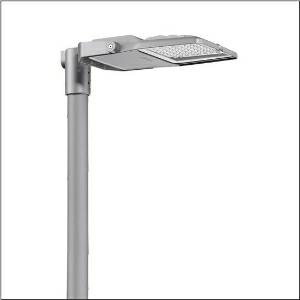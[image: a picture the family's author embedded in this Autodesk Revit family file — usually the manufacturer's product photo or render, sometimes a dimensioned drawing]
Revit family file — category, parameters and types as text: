
# Revit family: floodlight_fl_21_mini___pl52_5xa7776d2d3a_85e1
name_source: partatom
category: Lighting Fixtures
units: mm (PartAtom-declared; Revit-internal decimal feet)

## family parameters
Cut with Voids When Loaded = No
Host = Face
Light Source = No
Part Type = Normal
Room Calculation Point = No
Round Connector Dimension = Use Diameter
Shared = No

## types (1)
- --- (1 x LED, 17840 lm, 142.9 W, 3000K)
    Apparent Load = 143 VA
    CIE Flux Codes = 26 60 98 100 100
    Color Rendering = 70
    Color Temperature = 3000K
    Default Elevation = 1800 mm
    Description = Floodlight FL 21 mini, floodlight, primary light control with lens, of PMMA, primary optical cover: protective disc, of toughened safety glass, transparent, light distribution: PL52, light emission: direct distribution, installation type: surface-mounted, LED, High Power LED, rated luminous flux: 17.840lm, luminous efficacy: 125lm/W, light colour: 730, colour temperature: 3000K, control gear: ECG Smart Interface, control: flexible luminous flux parameterisation, time-dependent luminous flux control, constant luminous flux control, overheat protection, presetting dimming logarithmic, with terminal, 6-pole, mains connection: 220..240V, AC, 50/60Hz, start of lifetime: 143W, end of lifetime: 151W, reduction: 63W, luminaire housing, of diecast aluminium, powder-coated, Siteco® metallic grey (DB 702S), corrosivity category C5 according to DIN EN ISO 12944, mast bracket, of steel, galvanised, powder-coated, Siteco® metallic grey (DB 702S), protection rating (complete): IP66, insulation class (complete): insulation class II (safety insulation), certification: CE, protection symbol: D, impact resistance: IK08, permissible operating ambient temperature: -40..+40°C, permissible operating ambient temperature for outdoor applications: -40..+50°C, standard: DIN EN 12944, packaging unit: 1 piece

Light Distribution: PL52
    Height = 70 mm
    Lamp = 1 x LED
    Lamp Light Flux = 17840 lm
    Lamp Power = 142.9 W
    Lamp count = 1
    Length = 485 mm
    Luminous efficacy = 125 lm/W
    Manufacturer = Siteco
    ModVariant = No
    Model = 5XA7776D2D3A
    Number of Poles = 1
    OnlyDefault = Yes
    Power Factor = 1
    Product Name = Floodlight FL 21 mini | PL52
    Product group = floodlight | pylon top
    ProductGroupID = 6101
    Protection Class = Protection class II
    Protection Degree = IP 66
    RLX_Detail_Level = 1
    RlxData = <blob elided: 101285 chars, md5=bdc1c610>
    Socket = socket
    Standby Power = 0 W
    System Light Flux = 17840 lm
    System Power = 143 W
    Type Comments = factory setting: luminous flux: 100 % | dim-lin: 254 | 730 mA
    Type Image = l_1007125.jpg
    URL = http://relux.com
    VarID = @adj_074301
    Voltage = 0 V
    Weight = 0.00 kg
    Width = 337 mm

## geometry (parser evidence)
native form markers: Blend x4, Sweep x11
no freeform markers — native parametric forms only
